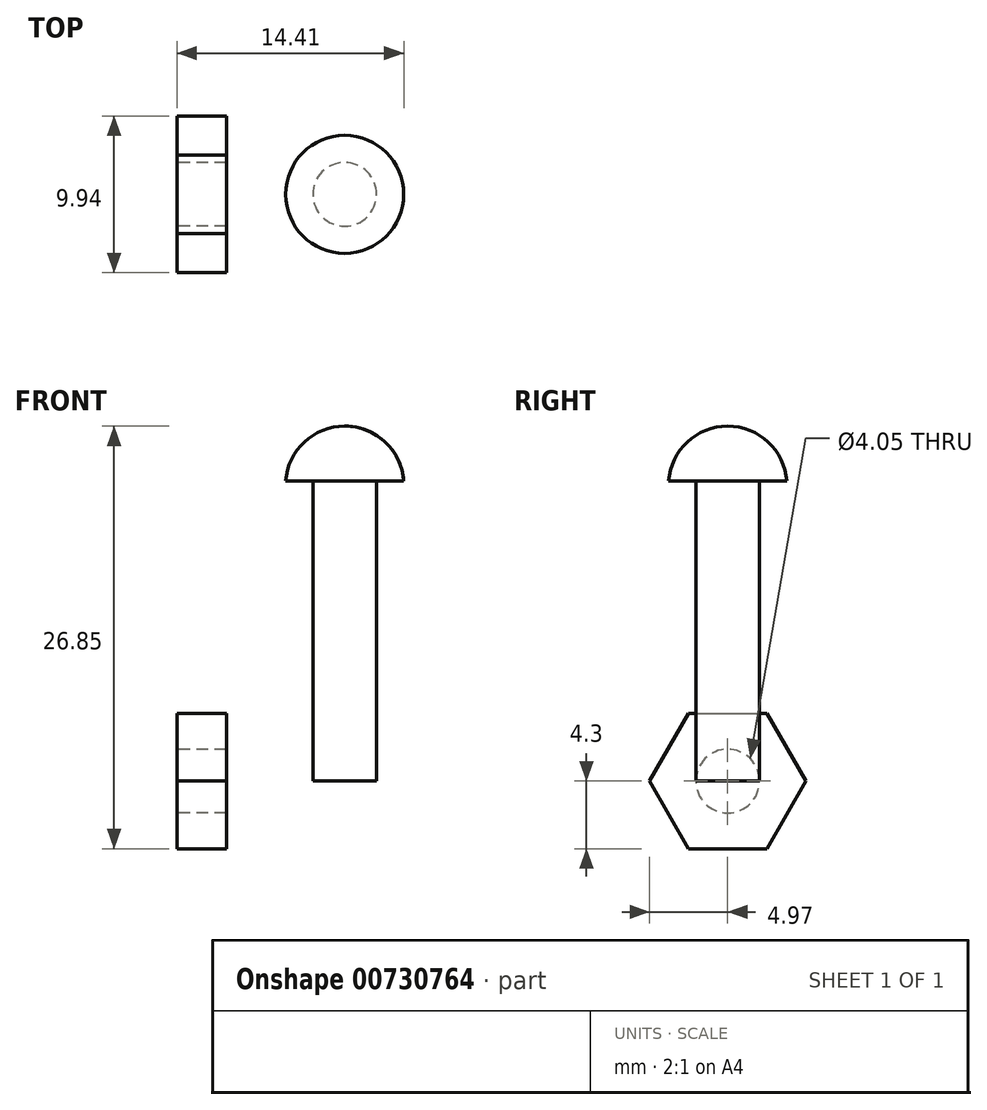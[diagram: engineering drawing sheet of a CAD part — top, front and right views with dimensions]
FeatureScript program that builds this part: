
annotation { "Feature Type Name" : "Feature", "Feature Type Description" : "" }
export const myFeature = defineFeature(function(context is Context, id is Id, definition is map)
    precondition{}
    {
        {
            var Q0;
            Q0=qCreatedBy(makeId("Right.planeOp"),FACE);
            var sketch = newSketch(context, id + "F0", { "sketchPlane" : qUnion([Q0])});
            skCircle(sketch, "E0.cCircle", {"center": v(0, 0) * mm, "radius": 4.3 * mm, "construction": true});
            skLineSegment(sketch, "E0.0", {"start": v(-4.97, 0) * mm, "end": v(-2.48, 4.3) * mm});
            skLineSegment(sketch, "E0.1", {"start": v(-2.48, 4.3) * mm, "end": v(2.48, 4.3) * mm});
            skLineSegment(sketch, "E0.2", {"start": v(2.48, 4.3) * mm, "end": v(4.97, 0) * mm});
            skLineSegment(sketch, "E0.3", {"start": v(4.97, 0) * mm, "end": v(2.48, -4.3) * mm});
            skLineSegment(sketch, "E0.4", {"start": v(2.48, -4.3) * mm, "end": v(-2.48, -4.3) * mm});
            skLineSegment(sketch, "E0.5", {"start": v(-2.48, -4.3) * mm, "end": v(-4.97, 0) * mm});
            skPoint(sketch, "E0.0.midPoint", {"position": v(-3.72, 2.15) * mm});
            skCircle(sketch, "E1", {"center": v(0, 0) * mm, "radius": 2.02 * mm});
            skSolve(sketch);
        }
        {
            var Q0;
            Q0=makeQuery(id+"F0.imprint","IMPRINT",FACE,{"disambiguationData":[TD([[makeQuery(id+"F0.imprint","IMPRINT",EDGE,{"derivedFrom":sQuery(id+"F0.wireOp",EDGE,"E0.0")}),-1.0]])]});
            extrude(context, id + "F1", {"entities" : qUnion([Q0]), "depth" : 3.14 * mm, "offsetDistance" : 25.4 * mm});
        }
        {
            var Q0;
            Q0=qCreatedBy(makeId("Front.planeOp"),FACE);
            var sketch = newSketch(context, id + "F2", { "sketchPlane" : qUnion([Q0])});
            skLineSegment(sketch, "E2", {"start": v(8.63, 0) * mm, "end": v(12.68, 0) * mm});
            skLineSegment(sketch, "E3", {"start": v(12.68, 0) * mm, "end": v(12.68, 19.05) * mm});
            skLineSegment(sketch, "E4", {"start": v(12.68, 19.05) * mm, "end": v(14.4, 19.05) * mm});
            skLineSegment(sketch, "E5", {"start": v(8.63, 0) * mm, "end": v(8.63, 19.05) * mm});
            skLineSegment(sketch, "E6", {"start": v(8.63, 19.05) * mm, "end": v(6.9, 19.05) * mm});
            skArc(sketch, "E7", {"start": v(14.4, 19.05) * mm, "mid": v(10.66, 22.55) * mm, "end": v(6.9, 19.05) * mm});
            skLineSegment(sketch, "E8", {"start": v(10.66, 22.55) * mm, "end": v(1.9, 22.55) * mm, "construction": true});
            skLineSegment(sketch, "E9", {"start": v(10.66, 22.55) * mm, "end": v(10.66, 0) * mm});
            skSolve(sketch);
        }
        {
            var Q0;
            {var subQ1=sQuery(id+"F2.wireOp",EDGE,"E3");Q0=makeQuery(id+"F2.imprint","IMPRINT",FACE,{"disambiguationData":[TD([[makeQuery(id+"F2.imprint","IMPRINT",EDGE,{"derivedFrom":subQ1}),1.0]])]});}
            var Q1;
            Q1=sQuery(id+"F2.wireOp",EDGE,"E9");
            revolve(context, id + "F3", {"surfaceOperationType" : NewSurfaceOperationType.NEW, "entities" : qUnion([Q0]), "axis" : qUnion([Q1]), "revolveType" : RevolveType.FULL});
        }
    });
